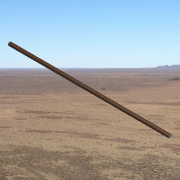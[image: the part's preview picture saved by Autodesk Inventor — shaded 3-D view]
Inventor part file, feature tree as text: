
AUTODESK INVENTOR PART (.ipt)
format: ipt  version: 2013 SP2 (Build 170200200, 200)  size: 124,416 bytes
history: native  units: in
note: dims shown in document units (in); Inventor stores cm internally (conversion verified against a paired STEP export)
features: extrude x1, sketch x1
ambient origin geometry x8: Origin, YZ Plane, XZ Plane, XY Plane, X Axis, Y Axis, Z Axis, Center Point
feature tree (2):
  extrude  "Extrusion2"  Depth=14.0in TaperAngle=0.0deg
  sketch  "Sketch2"  dims[d3=0.3in d4=14.0in d5=0.0in]
